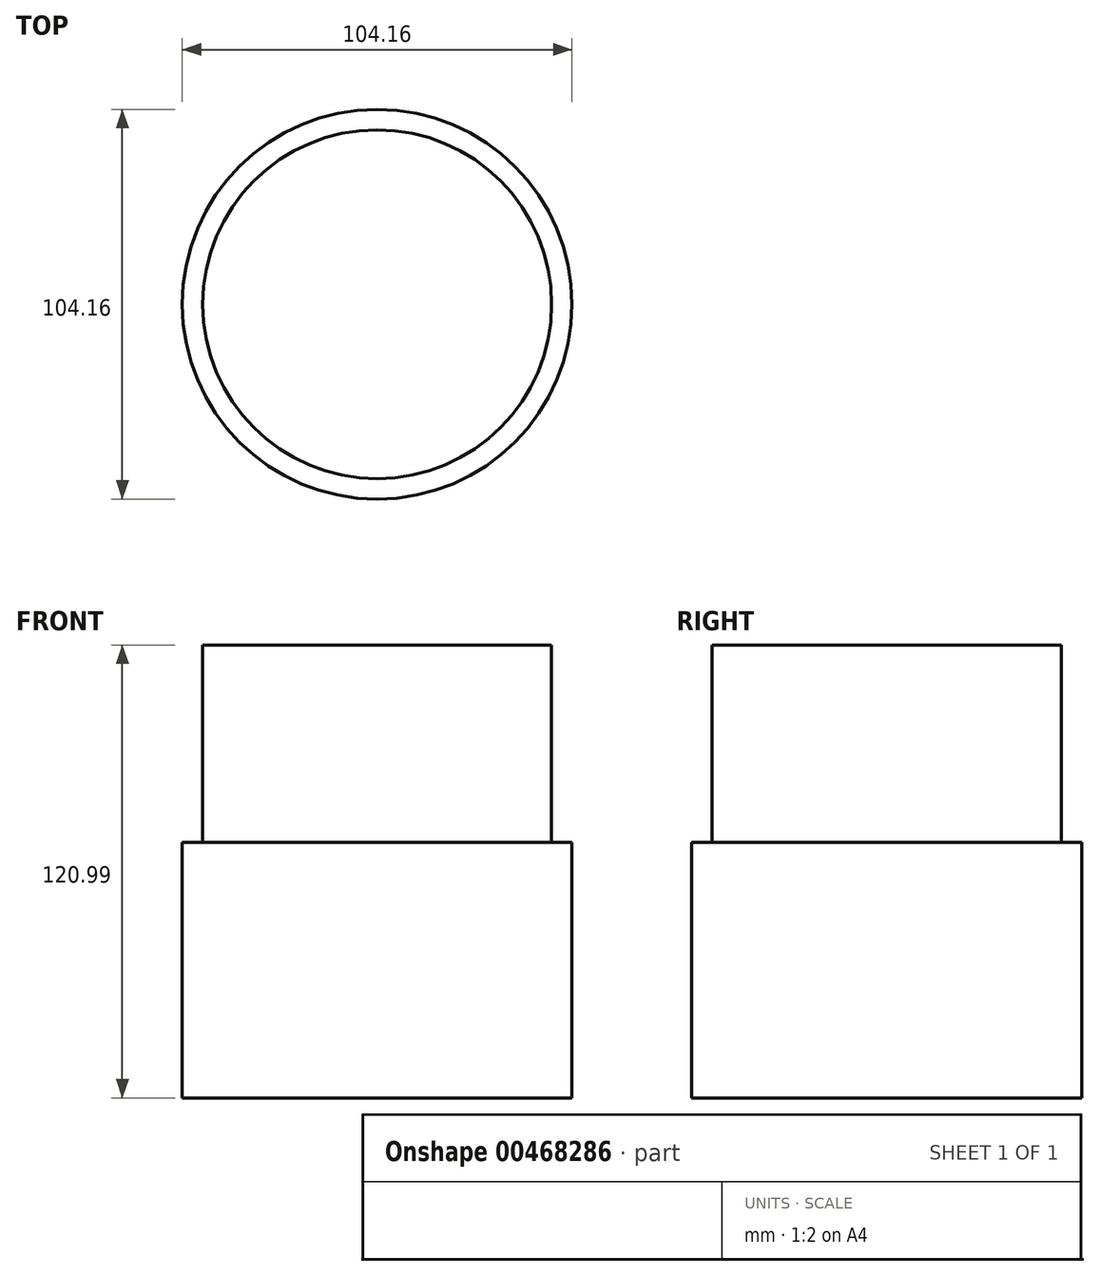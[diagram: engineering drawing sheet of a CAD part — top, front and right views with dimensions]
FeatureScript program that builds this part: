
annotation { "Feature Type Name" : "Feature", "Feature Type Description" : "" }
export const myFeature = defineFeature(function(context is Context, id is Id, definition is map)
    precondition{}
    {
        {
            var Q0;
            Q0=qCreatedBy(makeId("Top.planeOp"),FACE);
            var sketch = newSketch(context, id + "F0", { "sketchPlane" : qUnion([Q0])});
            skCircle(sketch, "E0", {"center": v(0, 0) * mm, "radius": 52.08 * mm});
            skSolve(sketch);
        }
        {
            var Q0;
            Q0=makeQuery(id+"F0.imprint","IMPRINT",FACE,{"disambiguationData":[TD([[makeQuery(id+"F0.imprint","IMPRINT",EDGE,{"derivedFrom":sQuery(id+"F0.wireOp",EDGE,"E0")}),1.0]])]});
            var Q1;
            Q1 = qSketchRegion(id + "F0", true);
            extrude(context, id + "F1", {"entities" : qUnion([Q0, Q1]), "depth" : 68.25 * mm});
        }
        {
            var Q0;
            Q0=makeQuery(id+"F1.opExtrude","CAP_FACE",FACE,{"disambiguationData":[OSD([sQuery(id+"F0.wireOp",EDGE,"E0")])],"isStart":false});
            var sketch = newSketch(context, id + "F2", { "sketchPlane" : qUnion([Q0])});
            skCircle(sketch, "E1.0", {"center": v(0, 0) * mm, "radius": 46.62 * mm});
            skSolve(sketch);
        }
        {
            var Q0;
            Q0=makeQuery(id+"F2.imprint","IMPRINT",FACE,{"disambiguationData":[TD([[makeQuery(id+"F2.imprint","IMPRINT",EDGE,{"derivedFrom":sQuery(id+"F2.wireOp",EDGE,"E1.0")}),1.0]])]});
            extrude(context, id + "F3", {"entities" : qUnion([Q0]), "operationType" : NewBodyOperationType.ADD, "depth" : 52.73 * mm});
        }
    });
